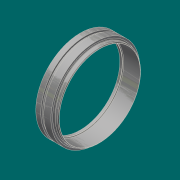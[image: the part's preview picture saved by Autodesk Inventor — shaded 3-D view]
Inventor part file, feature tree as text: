
AUTODESK INVENTOR PART (.ipt)
format: ipt  version: 2017.3 (Build 213257000, 257)  size: 240,128 bytes
history: native  units: in
note: dims shown in document units (in); Inventor stores cm internally (conversion verified against a paired STEP export)
features: revolve x1, chamfer x1, sketch x1
ambient origin geometry x8: Origin, YZ Plane, XZ Plane, XY Plane, X Axis, Y Axis, Z Axis, Center Point
bodies: Solid1 (feature_tree)
feature tree (3):
  revolve  "Revolution1"  [1 undecoded]
  chamfer  "Chamfer2"  Distance=0.3125in
  sketch  "Sketch1"  dims[d0=18.25in d3=17.0in d5=0.3125in d10=0.25in d12=16.25in d13=2.05in d16=90.0deg d17=0.375in d29=0.0312in d30=0.125in d31=45.0deg d35=1.0in d38=0.0687in d39=0.1374in d40=0.895in d41=0.6in d44=8.0in d45=0.2577in d47=0.375in d55=16.625in d58=0.5in d59=6.1875in]
note: 1 required parameter value undecoded (feature->parameter linkage not recoverable at this tier; creation-order binding heuristic only, values carry confidence <= 0.55)
